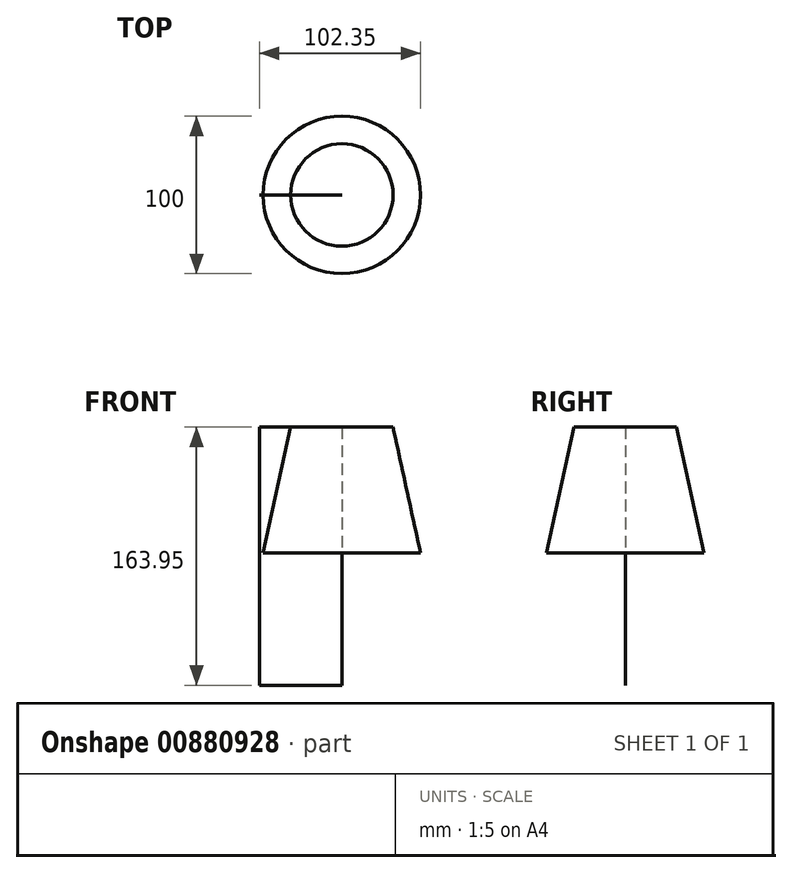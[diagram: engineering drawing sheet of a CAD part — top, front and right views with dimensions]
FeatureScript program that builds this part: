
annotation { "Feature Type Name" : "Feature", "Feature Type Description" : "" }
export const myFeature = defineFeature(function(context is Context, id is Id, definition is map)
    precondition{}
    {
        {
            var Q0;
            Q0=qCreatedBy(makeId("Top.planeOp"),FACE);
            var sketch = newSketch(context, id + "F0", { "sketchPlane" : qUnion([Q0])});
            skCircle(sketch, "E0", {"center": v(0, 0) * mm, "radius": 50 * mm});
            skSolve(sketch);
        }
        {
            var Q0;
            Q0=qCreatedBy(makeId("Top.planeOp"),FACE);
            cPlane(context, id + "F1", {"entities" : qUnion([Q0]), "cplaneType" : CPlaneType.OFFSET, "offset" : 80 * mm, "width" : 150 * mm, "height" : 150 * mm});
        }
        {
            var Q0;
            Q0=qCreatedBy(id+"F1.planeOp",FACE);
            var sketch = newSketch(context, id + "F2", { "sketchPlane" : qUnion([Q0])});
            skCircle(sketch, "E1", {"center": v(0, 0) * mm, "radius": 32.5 * mm});
            skSolve(sketch);
        }
        {
            var Q0;
            Q0 = qSketchRegion(id + "F0", true);
            var Q1;
            Q1 = qSketchRegion(id + "F2", true);
            var Q2;
            Q2 = qConstructionFilter(qBodyType(qCreatedBy(id + "F0" ,EDGE), BodyType.WIRE), ConstructionObject.NO);
            var Q3;
            Q3 = qConstructionFilter(qBodyType(qCreatedBy(id + "F2" ,EDGE), BodyType.WIRE), ConstructionObject.NO);
            loft(context, id + "F3", {"bodyType" : ToolBodyType.SURFACE, "sheetProfilesArray" : [{ "sheetProfileEntities" : qUnion([Q0]) }, { "sheetProfileEntities" : qUnion([Q1]) }], "wireProfilesArray" : [{ "wireProfileEntities" : qUnion([Q2]) }, { "wireProfileEntities" : qUnion([Q3]) }]});
        }
        {
            var Q0;
            Q0=qCreatedBy(id+"F1.planeOp",FACE);
            var sketch = newSketch(context, id + "F4", { "sketchPlane" : qUnion([Q0])});
            skLineSegment(sketch, "E2", {"start": v(0, 0) * mm, "end": v(-52.35, 0) * mm});
            skSolve(sketch);
        }
        {
            var Q0;
            Q0 = qSketchRegion(id + "F4", true);
            var Q1;
            Q1 = qConstructionFilter(qBodyType(qCreatedBy(id + "F4" ,EDGE), BodyType.WIRE), ConstructionObject.NO);
            extrude(context, id + "F5", {"entities" : qUnion([Q0]), "bodyType" : ToolBodyType.SURFACE, "surfaceEntities" : qUnion([Q1]), "endBound" : BoundingType.THROUGH_ALL, "oppositeDirection" : true, "depth" : 25 * mm, "offsetDistance" : 25 * mm, "hasDraft" : true, "draftAngle" : 3 * degree});
        }
    });
